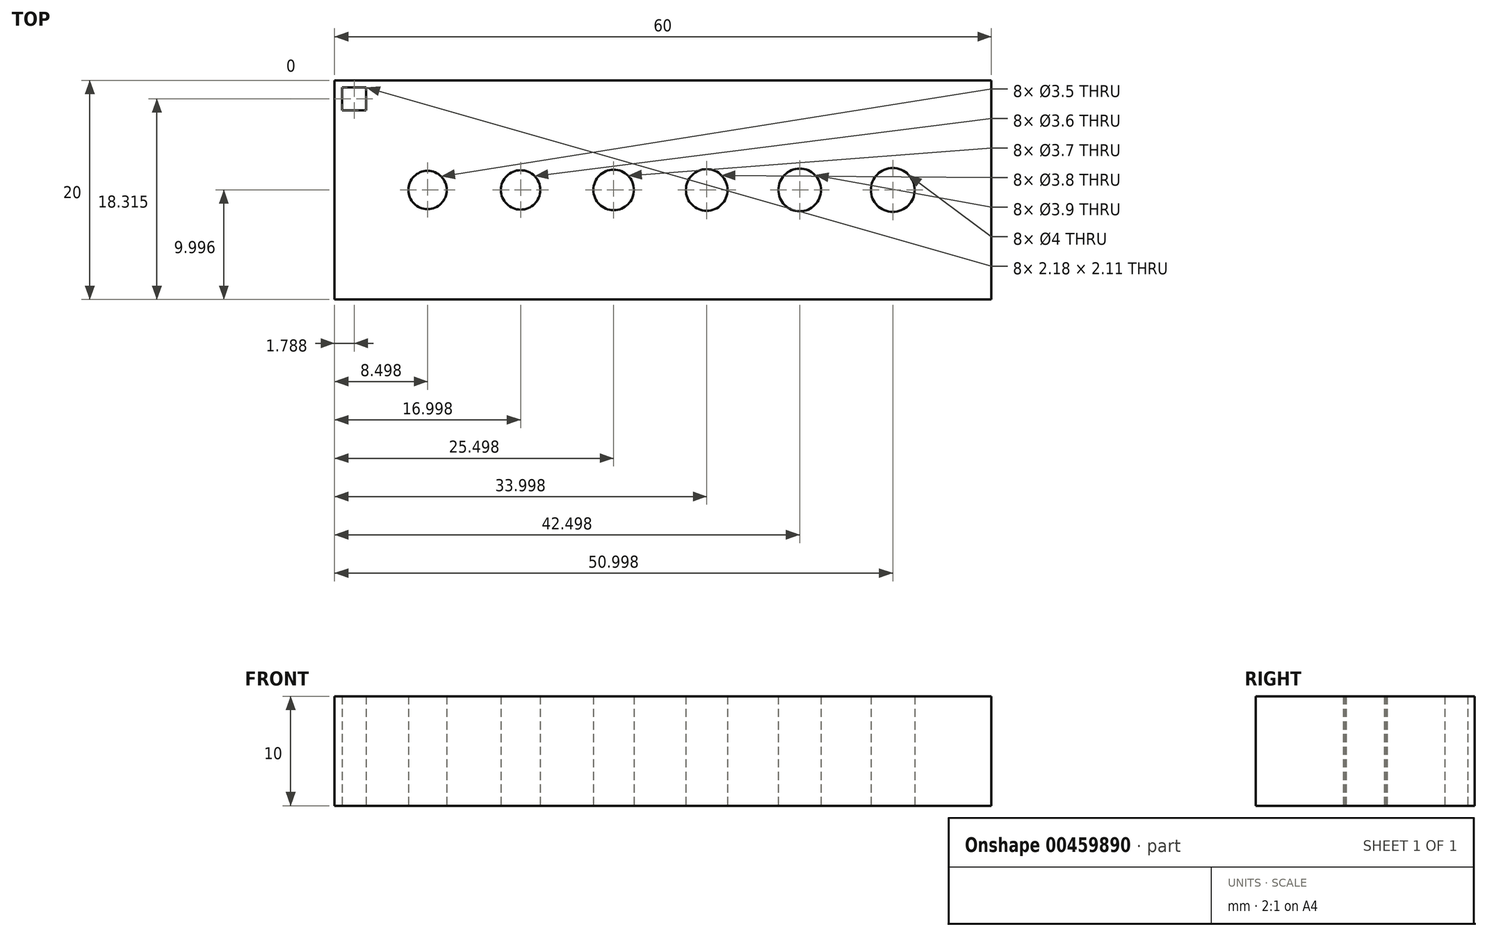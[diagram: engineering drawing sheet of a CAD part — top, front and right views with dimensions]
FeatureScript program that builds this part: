
annotation { "Feature Type Name" : "Feature", "Feature Type Description" : "" }
export const myFeature = defineFeature(function(context is Context, id is Id, definition is map)
    precondition{}
    {
        {
            var Q0;
            Q0=qCreatedBy(makeId("Top.planeOp"),FACE);
            var sketch = newSketch(context, id + "F0", { "sketchPlane" : qUnion([Q0])});
            skLineSegment(sketch, "E0.bottom", {"start": v(-14.72, -0.1) * mm, "end": v(45.28, -0.1) * mm});
            skLineSegment(sketch, "E0.top", {"start": v(-14.72, -20.1) * mm, "end": v(45.28, -20.1) * mm});
            skLineSegment(sketch, "E0.left", {"start": v(-14.72, -0.1) * mm, "end": v(-14.72, -20.1) * mm});
            skLineSegment(sketch, "E0.right", {"start": v(45.28, -0.1) * mm, "end": v(45.28, -20.1) * mm});
            skLineSegment(sketch, "E1", {"start": v(-14.72, -10.1) * mm, "end": v(45.28, -10.1) * mm, "construction": true});
            skCircle(sketch, "E2", {"center": v(-6.22, -10.1) * mm, "radius": 1.75 * mm});
            skCircle(sketch, "E3", {"center": v(2.28, -10.1) * mm, "radius": 1.8 * mm});
            skCircle(sketch, "E4", {"center": v(10.78, -10.1) * mm, "radius": 1.85 * mm});
            skCircle(sketch, "E5", {"center": v(19.28, -10.1) * mm, "radius": 1.9 * mm});
            skCircle(sketch, "E6", {"center": v(27.78, -10.1) * mm, "radius": 1.95 * mm});
            skCircle(sketch, "E7", {"center": v(36.28, -10.1) * mm, "radius": 2 * mm});
            skLineSegment(sketch, "E8.bottom", {"start": v(-14.02, -0.73) * mm, "end": v(-11.84, -0.73) * mm});
            skLineSegment(sketch, "E8.top", {"start": v(-14.02, -2.84) * mm, "end": v(-11.84, -2.84) * mm});
            skLineSegment(sketch, "E8.left", {"start": v(-14.02, -0.73) * mm, "end": v(-14.02, -2.84) * mm});
            skLineSegment(sketch, "E8.right", {"start": v(-11.84, -0.73) * mm, "end": v(-11.84, -2.84) * mm});
            skSolve(sketch);
        }
        {
            var Q0;
            Q0=makeQuery(id+"F0.imprint","IMPRINT",FACE,{"disambiguationData":[TD([[makeQuery(id+"F0.imprint","IMPRINT",EDGE,{"derivedFrom":sQuery(id+"F0.wireOp",EDGE,"E0.bottom")}),-1.0]])]});
            extrude(context, id + "F1", {"entities" : qUnion([Q0]), "depth" : 10 * mm});
        }
    });
